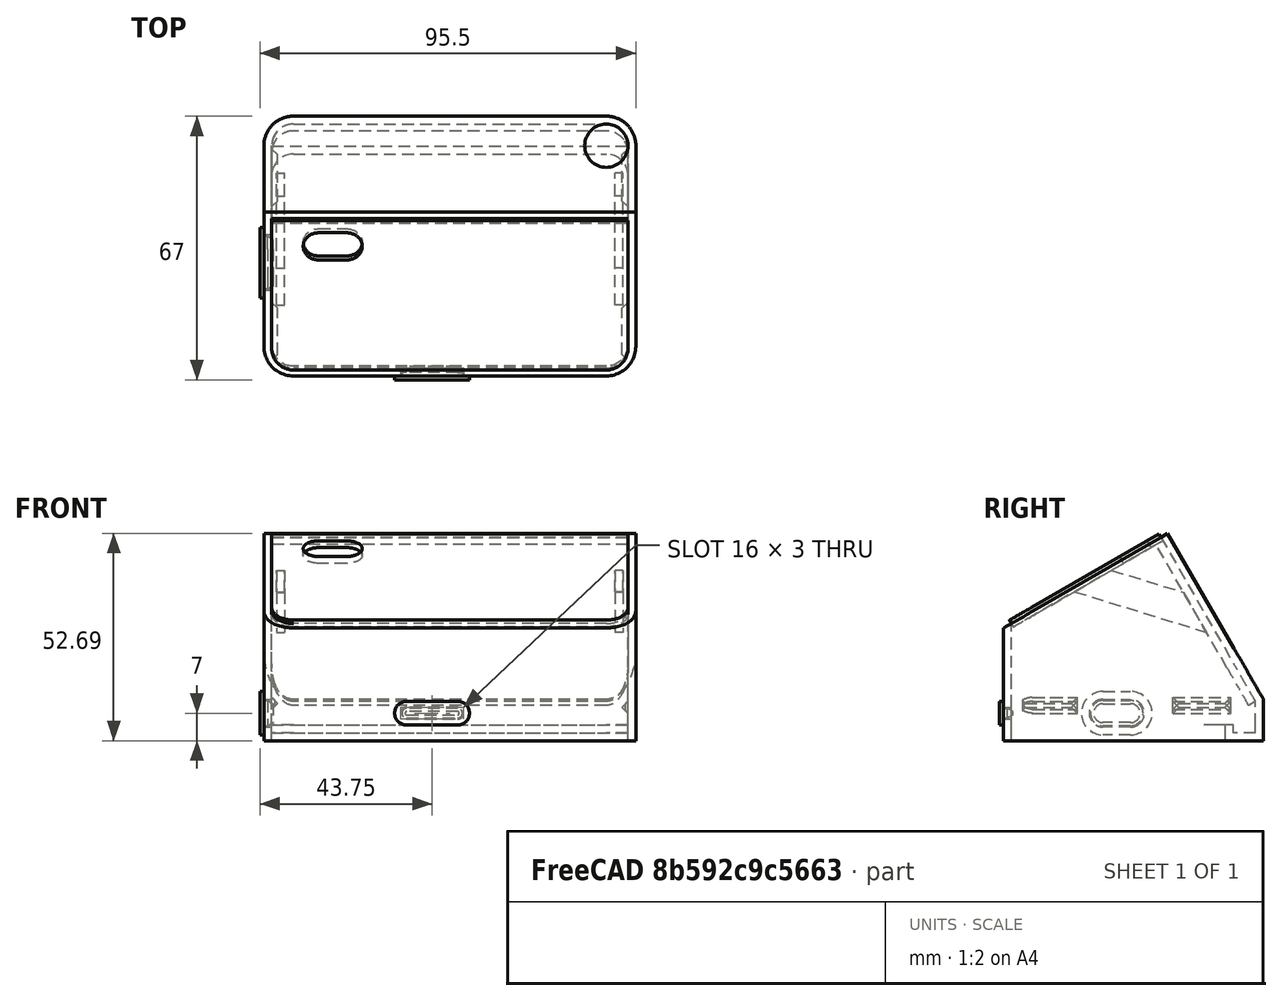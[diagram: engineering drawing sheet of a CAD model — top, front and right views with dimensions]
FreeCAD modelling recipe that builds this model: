
FCSTD DOCUMENT  (FreeCAD 0.21R33771 (Git))
Label: 2432S028_inner
License: All rights reserved
LicenseURL: http://en.wikipedia.org/wiki/All_rights_reserved
objects: Part::Extrusion×15, Sketcher::SketchObject×14, Part::Box×8, Part::Chamfer×6, Part::FeaturePython×6, Part::Cut×4, Mesh::Feature×4, Part::MultiCommon×2, Part::MultiFuse×1
note: 56 computed .brp shape members not serialized (recipe doc carries the construction recipe); baked Part::Feature solids carry a one-line shape summary decoded from their .brp

FEATURE [Sketcher::SketchObject] Sketch  label="Basis"
  FullyConstrained = true
  sketch-geometry (22):
    g0: LineSegment StartX=-39.75 StartY=33 StartZ=0 EndX=39.75 EndY=33 EndZ=0
    g1: LineSegment StartX=47.25 StartY=25.5 StartZ=0 EndX=47.25 EndY=-25.5 EndZ=0
    g2: LineSegment StartX=39.75 StartY=-33 StartZ=0 EndX=-39.75 EndY=-33 EndZ=0
    g3: LineSegment StartX=-47.25 StartY=-25.5 StartZ=0 EndX=-47.25 EndY=25.5 EndZ=0
    g4: ArcOfCircle CenterX=-39.75 CenterY=25.5 CenterZ=0 NormalX=0 NormalY=0 NormalZ=1 AngleXU=0 Radius=7.5 StartAngle=1.5708 EndAngle=3.14159
    g5: GeomPoint X=-47.25 Y=33 Z=0
    g6: ArcOfCircle CenterX=39.75 CenterY=25.5 CenterZ=0 NormalX=0 NormalY=0 NormalZ=1 AngleXU=0 Radius=7.5 StartAngle=0 EndAngle=1.5708
    g7: GeomPoint X=47.25 Y=33 Z=0
    g8: ArcOfCircle CenterX=39.75 CenterY=-25.5 CenterZ=0 NormalX=0 NormalY=0 NormalZ=1 AngleXU=0 Radius=7.5 StartAngle=4.71239 EndAngle=6.28319
    g9: GeomPoint X=47.25 Y=-33 Z=0
    g10: ArcOfCircle CenterX=-39.75 CenterY=-25.5 CenterZ=0 NormalX=0 NormalY=0 NormalZ=1 AngleXU=0 Radius=7.5 StartAngle=3.14159 EndAngle=4.71239
    g11: GeomPoint X=-47.25 Y=-33 Z=0
    g12: ArcOfCircle CenterX=39.75 CenterY=17.9 CenterZ=0 NormalX=0 NormalY=0 NormalZ=1 AngleXU=0 Radius=5.5 StartAngle=4e-16 EndAngle=1.5708
    g13: LineSegment StartX=45.25 StartY=17.9 StartZ=0 EndX=45.25 EndY=-25.5 EndZ=0
    g14: ArcOfCircle CenterX=39.75 CenterY=-25.5 CenterZ=0 NormalX=0 NormalY=0 NormalZ=1 AngleXU=0 Radius=5.5 StartAngle=4.71239 EndAngle=6.28319
    g15: LineSegment StartX=39.75 StartY=-31 StartZ=0 EndX=-39.75 EndY=-31 EndZ=0
    g16: ArcOfCircle CenterX=-39.75 CenterY=-25.5 CenterZ=0 NormalX=0 NormalY=0 NormalZ=1 AngleXU=0 Radius=5.5 StartAngle=3.14159 EndAngle=4.71239
    g17: LineSegment StartX=-45.25 StartY=-25.5 StartZ=0 EndX=-45.25 EndY=17.9 EndZ=0
    g18: ArcOfCircle CenterX=-39.75 CenterY=17.9 CenterZ=0 NormalX=0 NormalY=0 NormalZ=1 AngleXU=0 Radius=5.5 StartAngle=1.5708 EndAngle=3.14159
    g19: LineSegment StartX=-39.75 StartY=23.4 StartZ=0 EndX=39.75 EndY=23.4 EndZ=0
    g20: GeomPoint X=45.25 Y=23.4 Z=0
    g21: GeomPoint X=-45.25 Y=-31 Z=0
  constraints (50):
    c: Horizontal(g0)
    c: Horizontal(g2)
    c: Vertical(g1)
    c: Vertical(g3)
    c: DistanceY(g9,g7) = 66
    c: Symmetric(g5,g9,g-1)
    c: PointOnObject(g5,g0)
    c: PointOnObject(g5,g3)
    c: Tangent(g0,g4) = 1.5708
    c: Tangent(g3,g4) = 1.5708
    c: PointOnObject(g7,g0)
    c: PointOnObject(g7,g1)
    c: Tangent(g0,g6) = 1.5708
    c: Tangent(g1,g6) = 1.5708
    c: PointOnObject(g9,g1)
    c: PointOnObject(g9,g2)
    c: Tangent(g1,g8) = 1.5708
    c: Tangent(g2,g8) = 1.5708
    c: PointOnObject(g11,g2)
    c: PointOnObject(g11,g3)
    c: Tangent(g2,g10) = 1.5708
    c: Tangent(g3,g10) = 1.5708
    c: Equal(g8,g10)
    c: Equal(g10,g4)
    c: Equal(g4,g6)
    c: Tangent(g12,g13) = 1.5708
    c: Tangent(g13,g14) = 1.5708
    c: Tangent(g14,g15) = 1.5708
    c: Tangent(g15,g16) = 1.5708
    c: Tangent(g16,g17) = 1.5708
    c: Tangent(g17,g18) = 1.5708
    c: Tangent(g18,g19) = 1.5708
    c: Tangent(g19,g12) = 1.5708
    c: Horizontal(g15)
    c: Vertical(g13)
    c: Vertical(g17)
    c: Equal(g12,g14)
    c: Equal(g14,g16)
    c: Equal(g16,g18)
    c: PointOnObject(g20,g13)
    c: PointOnObject(g20,g19)
    c: PointOnObject(g21,g15)
    c: PointOnObject(g21,g17)
    c: DistanceY(g14,g12) = 54.4
    c: DistanceX(g17,g12) = 90.5
    c: Diameter(g12) = 11
    c: Symmetric(g12,g17,g-2)
    c: DistanceY(g2,g14) = 2
    c: Coincident(g10,g16)
    c: DistanceY(g18,g4) = 2.1
FEATURE [Part::Box] Box  label="Cube"
  AttacherType = Attacher::AttachEngine3D
  Height = 100
  Length = 100
  Placement = pos=(-50,39.3072,-0.4) rot=(1,0,0;0.523599rad)
  Width = 100
FEATURE [Sketcher::SketchObject] Sketch001
  ExternalGeometry = -> [Sketch]
  FullyConstrained = true
  sketch-geometry (20):
    g0: ArcOfCircle CenterX=-39.75 CenterY=25.5 CenterZ=0 NormalX=0 NormalY=0 NormalZ=1 AngleXU=0 Radius=7.5 StartAngle=1.5708 EndAngle=3.14159
    g1: LineSegment StartX=-39.75 StartY=33 StartZ=0 EndX=39.75 EndY=33 EndZ=0
    g2: ArcOfCircle CenterX=39.75 CenterY=25.5 CenterZ=0 NormalX=0 NormalY=0 NormalZ=1 AngleXU=0 Radius=7.5 StartAngle=1e-16 EndAngle=1.5708
    g3: LineSegment StartX=47.25 StartY=25.5 StartZ=0 EndX=47.25 EndY=-25.5 EndZ=0
    g4: ArcOfCircle CenterX=39.75 CenterY=-25.5 CenterZ=0 NormalX=0 NormalY=0 NormalZ=1 AngleXU=0 Radius=7.5 StartAngle=4.71239 EndAngle=6.28319
    g5: LineSegment StartX=39.75 StartY=-33 StartZ=0 EndX=-39.75 EndY=-33 EndZ=0
    g6: ArcOfCircle CenterX=-39.75 CenterY=-25.5 CenterZ=0 NormalX=0 NormalY=0 NormalZ=1 AngleXU=0 Radius=7.5 StartAngle=3.14159 EndAngle=4.71239
    g7: LineSegment StartX=-47.25 StartY=-25.5 StartZ=0 EndX=-47.25 EndY=25.5 EndZ=0
    g8: GeomPoint X=-47.25 Y=33 Z=0
    g9: GeomPoint X=47.25 Y=-33 Z=0
    g10: ArcOfCircle CenterX=-39.75 CenterY=17.9 CenterZ=0 NormalX=0 NormalY=0 NormalZ=1 AngleXU=0 Radius=5.5 StartAngle=1.5708 EndAngle=3.14159
    g11: LineSegment StartX=-39.75 StartY=23.4 StartZ=0 EndX=39.75 EndY=23.4 EndZ=0
    g12: ArcOfCircle CenterX=39.75 CenterY=17.9 CenterZ=0 NormalX=0 NormalY=0 NormalZ=1 AngleXU=0 Radius=5.5 StartAngle=0 EndAngle=1.5708
    g13: LineSegment StartX=45.25 StartY=17.9 StartZ=0 EndX=45.25 EndY=-25.5 EndZ=0
    g14: ArcOfCircle CenterX=39.75 CenterY=-25.5 CenterZ=0 NormalX=0 NormalY=0 NormalZ=1 AngleXU=0 Radius=5.5 StartAngle=4.71239 EndAngle=6.28319
    g15: LineSegment StartX=39.75 StartY=-31 StartZ=0 EndX=-39.75 EndY=-31 EndZ=0
    g16: ArcOfCircle CenterX=-39.75 CenterY=-25.5 CenterZ=0 NormalX=0 NormalY=0 NormalZ=1 AngleXU=0 Radius=5.5 StartAngle=3.14159 EndAngle=4.71239
    g17: LineSegment StartX=-45.25 StartY=-25.5 StartZ=0 EndX=-45.25 EndY=17.9 EndZ=0
    g18: GeomPoint X=-45.25 Y=23.4 Z=0
    g19: GeomPoint X=45.25 Y=-31 Z=0
  constraints (44):
    c: Tangent(g0,g1) = 1.5708
    c: Tangent(g1,g2) = 1.5708
    c: Tangent(g2,g3) = 1.5708
    c: Tangent(g3,g4) = 1.5708
    c: Tangent(g4,g5) = 1.5708
    c: Tangent(g5,g6) = 1.5708
    c: Tangent(g6,g7) = 1.5708
    c: Tangent(g7,g0) = 1.5708
    c: Horizontal(g1)
    c: Horizontal(g5)
    c: Vertical(g3)
    c: Vertical(g7)
    c: Equal(g0,g2)
    c: Equal(g2,g4)
    c: Equal(g4,g6)
    c: PointOnObject(g8,g1)
    c: PointOnObject(g8,g7)
    c: PointOnObject(g9,g3)
    c: PointOnObject(g9,g5)
    c: Coincident(g-6,g4)
    c: Coincident(g0,g-3)
    c: Horizontal(g-3,g0)
    c: Tangent(g10,g11) = 1.5708
    c: Tangent(g11,g12) = 1.5708
    c: Tangent(g12,g13) = 1.5708
    c: Tangent(g13,g14) = 1.5708
    c: Tangent(g14,g15) = 1.5708
    c: Tangent(g15,g16) = 1.5708
    c: Tangent(g16,g17) = 1.5708
    c: Tangent(g17,g10) = 1.5708
    c: Horizontal(g11)
    c: Horizontal(g15)
    c: Vertical(g13)
    c: Vertical(g17)
    c: Equal(g10,g12)
    c: Equal(g12,g14)
    c: Equal(g14,g16)
    c: PointOnObject(g18,g11)
    c: PointOnObject(g18,g17)
    c: PointOnObject(g19,g13)
    c: PointOnObject(g19,g15)
    c: Coincident(g14,g4)
    c: Coincident(g10,g-5)
    c: Horizontal(g-5,g10)
FEATURE [Part::Extrusion] Extrude
  Base = -> Sketch001
  Dir = (0,0,1)
  DirMode = 2
  FaceMakerClass = Part::FaceMakerBullseye
  LengthFwd = 2
  LengthRev = 0
  Solid = true
  Symmetric = false
FEATURE [Sketcher::SketchObject] Sketch002
  ExternalGeometry = -> [Sketch]
  FullyConstrained = true
  Placement = pos=(0,0,2) rot=(0,0,1;0rad)
  sketch-geometry (26):
    g0: ArcOfCircle CenterX=-39.75 CenterY=25.5 CenterZ=0 NormalX=0 NormalY=0 NormalZ=1 AngleXU=0 Radius=7.5 StartAngle=1.5708 EndAngle=3.14159
    g1: LineSegment StartX=-39.75 StartY=33 StartZ=0 EndX=39.75 EndY=33 EndZ=0
    g2: ArcOfCircle CenterX=39.75 CenterY=25.5 CenterZ=0 NormalX=0 NormalY=0 NormalZ=1 AngleXU=0 Radius=7.5 StartAngle=4e-16 EndAngle=1.5708
    g3: LineSegment StartX=47.25 StartY=25.5 StartZ=0 EndX=47.25 EndY=-25.5 EndZ=0
    g4: ArcOfCircle CenterX=39.75 CenterY=-25.5 CenterZ=0 NormalX=0 NormalY=0 NormalZ=1 AngleXU=0 Radius=7.5 StartAngle=4.71239 EndAngle=6.28319
    g5: LineSegment StartX=39.75 StartY=-33 StartZ=0 EndX=-39.75 EndY=-33 EndZ=0
    g6: ArcOfCircle CenterX=-39.75 CenterY=-25.5 CenterZ=0 NormalX=0 NormalY=0 NormalZ=1 AngleXU=0 Radius=7.5 StartAngle=3.14159 EndAngle=4.71239
    g7: LineSegment StartX=-47.25 StartY=-25.5 StartZ=0 EndX=-47.25 EndY=25.5 EndZ=0
    g8: GeomPoint X=-47.25 Y=33 Z=0
    g9: GeomPoint X=47.25 Y=-33 Z=0
    g10: ArcOfCircle CenterX=-39.75 CenterY=17.9 CenterZ=0 NormalX=0 NormalY=0 NormalZ=1 AngleXU=0 Radius=5.5 StartAngle=1.5708 EndAngle=3.14159
    g11: LineSegment StartX=-39.75 StartY=23.4 StartZ=0 EndX=39.75 EndY=23.4 EndZ=0
    g12: ArcOfCircle CenterX=39.75 CenterY=17.9 CenterZ=0 NormalX=0 NormalY=0 NormalZ=1 AngleXU=0 Radius=5.5 StartAngle=0 EndAngle=1.5708
    g13: LineSegment StartX=45.25 StartY=17.9 StartZ=0 EndX=45.25 EndY=-25.5 EndZ=0
    g14: ArcOfCircle CenterX=39.75 CenterY=-25.5 CenterZ=0 NormalX=0 NormalY=0 NormalZ=1 AngleXU=0 Radius=5.5 StartAngle=4.71239 EndAngle=6.28319
    g15: LineSegment StartX=39.75 StartY=-31 StartZ=0 EndX=-39.75 EndY=-31 EndZ=0
    g16: ArcOfCircle CenterX=-39.75 CenterY=-25.5 CenterZ=0 NormalX=0 NormalY=0 NormalZ=1 AngleXU=0 Radius=5.5 StartAngle=3.14159 EndAngle=4.71239
    g17: LineSegment StartX=-45.25 StartY=-25.5 StartZ=0 EndX=-45.25 EndY=17.9 EndZ=0
    g18: GeomPoint X=-45.25 Y=23.4 Z=0
    g19: GeomPoint X=45.25 Y=-31 Z=0
    g20: ArcOfCircle CenterX=-39.75 CenterY=25.5 CenterZ=0 NormalX=0 NormalY=0 NormalZ=1 AngleXU=0 Radius=5.5 StartAngle=1.5708 EndAngle=3.14159
    g21: LineSegment StartX=-39.75 StartY=31 StartZ=0 EndX=39.75 EndY=31 EndZ=0
    g22: ArcOfCircle CenterX=39.75 CenterY=25.5 CenterZ=0 NormalX=0 NormalY=0 NormalZ=1 AngleXU=0 Radius=5.5 StartAngle=0 EndAngle=1.5708
    g23: LineSegment StartX=-45.25 StartY=25.4 StartZ=0 EndX=45.25 EndY=25.4 EndZ=0
    g24: LineSegment StartX=-45.25 StartY=25.5 StartZ=0 EndX=-45.25 EndY=25.4 EndZ=0
    g25: LineSegment StartX=45.25 StartY=25.5 StartZ=0 EndX=45.25 EndY=25.4 EndZ=0
  constraints (62):
    c: Tangent(g0,g1) = 1.5708
    c: Tangent(g1,g2) = 1.5708
    c: Tangent(g2,g3) = 1.5708
    c: Tangent(g3,g4) = 1.5708
    c: Tangent(g4,g5) = 1.5708
    c: Tangent(g5,g6) = 1.5708
    c: Tangent(g6,g7) = 1.5708
    c: Tangent(g7,g0) = 1.5708
    c: Horizontal(g1)
    c: Horizontal(g5)
    c: Vertical(g3)
    c: Vertical(g7)
    c: Equal(g0,g2)
    c: Equal(g2,g4)
    c: Equal(g4,g6)
    c: PointOnObject(g8,g1)
    c: PointOnObject(g8,g7)
    c: PointOnObject(g9,g3)
    c: PointOnObject(g9,g5)
    c: Coincident(g4,g-6)
    c: Coincident(g0,g-3)
    c: Horizontal(g-3,g0)
    c: Tangent(g10,g11) = 1.5708
    c: Tangent(g11,g12) = 1.5708
    c: Tangent(g12,g13) = 1.5708
    c: Tangent(g13,g14) = 1.5708
    c: Tangent(g14,g15) = 1.5708
    c: Tangent(g15,g16) = 1.5708
    c: Tangent(g16,g17) = 1.5708
    c: Tangent(g17,g10) = 1.5708
    c: Horizontal(g11)
    c: Horizontal(g15)
    c: Vertical(g13)
    c: Vertical(g17)
    c: Equal(g10,g12)
    c: Equal(g12,g14)
    c: Equal(g14,g16)
    c: PointOnObject(g18,g11)
    c: PointOnObject(g18,g17)
    c: PointOnObject(g19,g13)
    c: PointOnObject(g19,g15)
    c: Coincident(g4,g14)
    c: Coincident(g10,g-5)
    c: Horizontal(g14,g-6)
    c: Coincident(g20,g0)
    c: Vertical(g0,g20)
    c: Horizontal(g0,g20)
    c: DistanceY(g20,g0) = 2
    c: Coincident(g21,g20)
    c: Horizontal(g21)
    c: Coincident(g22,g2)
    c: Coincident(g22,g21)
    c: Equal(g22,g20)
    c: Horizontal(g2,g22)
    c: Horizontal(g23)
    c: Coincident(g24,g20)
    c: Coincident(g24,g23)
    c: Vertical(g24)
    c: Coincident(g25,g22)
    c: Coincident(g25,g23)
    c: Vertical(g25)
    c: DistanceY(g10,g23) = 2
FEATURE [Part::Extrusion] Extrude001  label="Extrude_2mm"
  Base = -> Sketch002
  Dir = (0,0,1)
  DirMode = 2
  FaceMakerClass = Part::FaceMakerBullseye
  LengthFwd = 2
  LengthRev = 0
  Solid = true
  Symmetric = false
FEATURE [Sketcher::SketchObject] Sketch003
  ExternalGeometry = -> [Sketch]
  FullyConstrained = true
  Placement = pos=(0,0,4) rot=(0,0,1;0rad)
  sketch-geometry (20):
    g0: ArcOfCircle CenterX=-39.75 CenterY=25.5 CenterZ=0 NormalX=0 NormalY=0 NormalZ=1 AngleXU=0 Radius=7.5 StartAngle=1.5708 EndAngle=3.14159
    g1: LineSegment StartX=-39.75 StartY=33 StartZ=0 EndX=39.75 EndY=33 EndZ=0
    g2: ArcOfCircle CenterX=39.75 CenterY=25.5 CenterZ=0 NormalX=0 NormalY=0 NormalZ=1 AngleXU=0 Radius=7.5 StartAngle=0 EndAngle=1.5708
    g3: LineSegment StartX=47.25 StartY=25.5 StartZ=0 EndX=47.25 EndY=-25.5 EndZ=0
    g4: ArcOfCircle CenterX=39.75 CenterY=-25.5 CenterZ=0 NormalX=0 NormalY=0 NormalZ=1 AngleXU=0 Radius=7.5 StartAngle=4.71239 EndAngle=6.28319
    g5: LineSegment StartX=39.75 StartY=-33 StartZ=0 EndX=-39.75 EndY=-33 EndZ=0
    g6: ArcOfCircle CenterX=-39.75 CenterY=-25.5 CenterZ=0 NormalX=0 NormalY=0 NormalZ=1 AngleXU=0 Radius=7.5 StartAngle=3.14159 EndAngle=4.71239
    g7: LineSegment StartX=-47.25 StartY=-25.5 StartZ=0 EndX=-47.25 EndY=25.5 EndZ=0
    g8: GeomPoint X=-47.25 Y=33 Z=0
    g9: GeomPoint X=47.25 Y=-33 Z=0
    g10: ArcOfCircle CenterX=-39.75 CenterY=25.5 CenterZ=0 NormalX=0 NormalY=0 NormalZ=1 AngleXU=0 Radius=5.5 StartAngle=1.5708 EndAngle=3.14159
    g11: LineSegment StartX=-39.75 StartY=31 StartZ=0 EndX=39.75 EndY=31 EndZ=0
    g12: ArcOfCircle CenterX=39.75 CenterY=25.5 CenterZ=0 NormalX=0 NormalY=0 NormalZ=1 AngleXU=0 Radius=5.5 StartAngle=0 EndAngle=1.5708
    g13: LineSegment StartX=45.25 StartY=25.5 StartZ=0 EndX=45.25 EndY=-25.5 EndZ=0
    g14: ArcOfCircle CenterX=39.75 CenterY=-25.5 CenterZ=0 NormalX=0 NormalY=0 NormalZ=1 AngleXU=0 Radius=5.5 StartAngle=4.71239 EndAngle=6.28319
    g15: LineSegment StartX=39.75 StartY=-31 StartZ=0 EndX=-39.75 EndY=-31 EndZ=0
    g16: ArcOfCircle CenterX=-39.75 CenterY=-25.5 CenterZ=0 NormalX=0 NormalY=0 NormalZ=1 AngleXU=0 Radius=5.5 StartAngle=3.14159 EndAngle=4.71239
    g17: LineSegment StartX=-45.25 StartY=-25.5 StartZ=0 EndX=-45.25 EndY=25.5 EndZ=0
    g18: GeomPoint X=-45.25 Y=31 Z=0
    g19: GeomPoint X=45.25 Y=-31 Z=0
  constraints (45):
    c: Tangent(g0,g1) = 1.5708
    c: Tangent(g1,g2) = 1.5708
    c: Tangent(g2,g3) = 1.5708
    c: Tangent(g3,g4) = 1.5708
    c: Tangent(g4,g5) = 1.5708
    c: Tangent(g5,g6) = 1.5708
    c: Tangent(g6,g7) = 1.5708
    c: Tangent(g7,g0) = 1.5708
    c: Horizontal(g1)
    c: Horizontal(g5)
    c: Vertical(g3)
    c: Vertical(g7)
    c: Equal(g0,g2)
    c: Equal(g2,g4)
    c: Equal(g4,g6)
    c: PointOnObject(g8,g1)
    c: PointOnObject(g8,g7)
    c: PointOnObject(g9,g3)
    c: PointOnObject(g9,g5)
    c: Coincident(g-5,g4)
    c: Coincident(g0,g-3)
    c: Horizontal(g-3,g0)
    c: Tangent(g10,g11) = 1.5708
    c: Tangent(g12,g13) = 1.5708
    c: Tangent(g13,g14) = 1.5708
    c: Tangent(g14,g15) = 1.5708
    c: Tangent(g15,g16) = 1.5708
    c: Tangent(g16,g17) = 1.5708
    c: Tangent(g17,g10) = 1.5708
    c: Horizontal(g11)
    c: Horizontal(g15)
    c: Vertical(g13)
    c: Vertical(g17)
    c: Equal(g10,g12)
    c: Equal(g12,g14)
    c: Equal(g14,g16)
    c: PointOnObject(g18,g11)
    c: PointOnObject(g18,g17)
    c: PointOnObject(g19,g13)
    c: PointOnObject(g19,g15)
    c: Coincident(g14,g4)
    c: Coincident(g11,g12)
    c: Coincident(g0,g10)
    c: Horizontal(g15,g-6)
    c: Vertical(g12,g11)
FEATURE [Part::Extrusion] Extrude002  label="Extrude_4mm"
  Base = -> Sketch003
  Dir = (0,0,1)
  DirMode = 2
  FaceMakerClass = Part::FaceMakerBullseye
  LengthFwd = 10
  LengthRev = 0
  Solid = true
  Symmetric = false
FEATURE [Part::Extrusion] Extrude003  label="Extrude_6mm"
  Base = -> Sketch003
  Dir = (0,0,1)
  DirMode = 2
  FaceMakerClass = Part::FaceMakerBullseye
  LengthFwd = 52
  LengthRev = 0
  Solid = true
  Symmetric = false
FEATURE [Part::Box] Box001  label="Cube001"
  AttacherType = Attacher::AttachEngine3D
  Height = 100
  Length = 100
  Placement = pos=(-50,-49.5397,19.0874) rot=(1,0,0;0.523599rad)
  Width = 100
FEATURE [Part::Box] Box002  label="Cube002"
  AttacherType = Attacher::AttachEngine3D
  Height = 100
  Length = 100
  Placement = pos=(-50,37.5751,-1.4) rot=(1,0,0;0.523599rad)
  Width = 2
FEATURE [Sketcher::SketchObject] Sketch004
  ExternalGeometry = -> [Sketch]
  FullyConstrained = false
  sketch-geometry (12):
    g0: ArcOfCircle CenterX=-39.75 CenterY=25.5 CenterZ=0 NormalX=0 NormalY=0 NormalZ=1 AngleXU=0 Radius=7.5 StartAngle=1.5708 EndAngle=3.14159
    g1: LineSegment StartX=-39.75 StartY=33 StartZ=0 EndX=39.75 EndY=33 EndZ=0
    g2: ArcOfCircle CenterX=39.75 CenterY=25.5 CenterZ=0 NormalX=0 NormalY=0 NormalZ=1 AngleXU=0 Radius=7.5 StartAngle=1e-16 EndAngle=1.5708
    g3: LineSegment StartX=47.25 StartY=25.5 StartZ=0 EndX=47.25 EndY=-25.5 EndZ=0
    g4: ArcOfCircle CenterX=39.75 CenterY=-25.5 CenterZ=0 NormalX=0 NormalY=0 NormalZ=1 AngleXU=0 Radius=7.5 StartAngle=4.71239 EndAngle=6.28319
    g5: LineSegment StartX=39.75 StartY=-33 StartZ=0 EndX=-39.75 EndY=-33 EndZ=0
    g6: ArcOfCircle CenterX=-39.75 CenterY=-25.5 CenterZ=0 NormalX=0 NormalY=0 NormalZ=1 AngleXU=0 Radius=7.5 StartAngle=3.14159 EndAngle=4.71239
    g7: LineSegment StartX=-47.25 StartY=-25.5 StartZ=0 EndX=-47.25 EndY=25.5 EndZ=0
    g8: GeomPoint X=-47.25 Y=33 Z=0
    g9: GeomPoint X=47.25 Y=-33 Z=0
    g10: GeomPoint X=-22 Y=14 Z=0
    g11: GeomPoint X=22 Y=-30 Z=0
  constraints (22):
    c: Tangent(g0,g1) = 1.5708
    c: Tangent(g1,g2) = 1.5708
    c: Tangent(g2,g3) = 1.5708
    c: Tangent(g3,g4) = 1.5708
    c: Tangent(g4,g5) = 1.5708
    c: Tangent(g5,g6) = 1.5708
    c: Tangent(g6,g7) = 1.5708
    c: Tangent(g7,g0) = 1.5708
    c: Horizontal(g1)
    c: Horizontal(g5)
    c: Vertical(g3)
    c: Vertical(g7)
    c: Equal(g0,g2)
    c: Equal(g2,g4)
    c: Equal(g4,g6)
    c: PointOnObject(g8,g1)
    c: PointOnObject(g8,g7)
    c: PointOnObject(g9,g3)
    c: PointOnObject(g9,g5)
    c: Coincident(g0,g-3)
    c: Horizontal(g-3,g0)
    c: Coincident(g4,g-4)
FEATURE [Part::Extrusion] Extrude004
  Base = -> Sketch004
  Dir = (0,0,1)
  DirMode = 2
  FaceMakerClass = Part::FaceMakerBullseye
  LengthFwd = 56
  LengthRev = 0
  Solid = true
  Symmetric = false
FEATURE [Part::MultiCommon] Common
  Shapes = -> [Box002,Extrude004]
FEATURE [Part::MultiFuse] Fusion
  Shapes = -> [Common,Extrude,Extrude001,Extrude002,Extrude003]
FEATURE [Part::Cut] Cut
  Base = -> Fusion
  Tool = -> Box
FEATURE [Part::Cut] Cut001
  Base = -> Cut
  Tool = -> Box001
FEATURE [Part::Box] Box003  label="Cube003"
  AttacherType = Attacher::AttachEngine3D
  Height = 3
  Length = 1.5
  Placement = pos=(43.75,-29,7) rot=(0,0,1;0rad)
  Width = 14.7
FEATURE [Part::Chamfer] Chamfer
  Base = -> Box003
  Edges = 4 edges r=1.49: [Edge1,Edge2,Edge3,Edge4]
FEATURE [Part::Box] Box004  label="Cube004"
  AttacherType = Attacher::AttachEngine3D
  Height = 3
  Length = 1.5
  Placement = pos=(-45.25,-29,8) rot=(0,0,1;0rad)
  Width = 14.7
FEATURE [Part::Chamfer] Chamfer001
  Base = -> Box004
  Edges = 4 edges r=1.49: [Edge5,Edge6,Edge7,Edge8]
FEATURE [Sketcher::SketchObject] Sketch005  label="Basis001_bEZEL"
  FullyConstrained = true
  Placement = pos=(0,-2.75,0) rot=(0,1,0;3.14159rad)
  sketch-geometry (46):
    g0: ArcOfCircle CenterX=40 CenterY=22 CenterZ=0 NormalX=0 NormalY=0 NormalZ=1 AngleXU=0 Radius=3 StartAngle=4e-16 EndAngle=1.5708
    g1: LineSegment StartX=43 StartY=22 StartZ=0 EndX=43 EndY=-22 EndZ=0
    g2: ArcOfCircle CenterX=40 CenterY=-22 CenterZ=0 NormalX=0 NormalY=0 NormalZ=1 AngleXU=0 Radius=3 StartAngle=4.71239 EndAngle=6.28319
    g3: LineSegment StartX=40 StartY=-25 StartZ=0 EndX=-40 EndY=-25 EndZ=0
    g4: ArcOfCircle CenterX=-40 CenterY=-22 CenterZ=0 NormalX=0 NormalY=0 NormalZ=1 AngleXU=0 Radius=3 StartAngle=3.14159 EndAngle=4.71239
    g5: LineSegment StartX=-43 StartY=-22 StartZ=0 EndX=-43 EndY=22 EndZ=0
    g6: ArcOfCircle CenterX=-40 CenterY=22 CenterZ=0 NormalX=0 NormalY=0 NormalZ=1 AngleXU=0 Radius=3 StartAngle=1.5708 EndAngle=3.14159
    g7: LineSegment StartX=-40 StartY=25 StartZ=0 EndX=40 EndY=25 EndZ=0
    g8: GeomPoint X=43 Y=25 Z=0
    g9: GeomPoint X=-43 Y=-25 Z=0
    g10: Circle CenterX=-39 CenterY=21 CenterZ=0 NormalX=0 NormalY=0 NormalZ=1 AngleXU=0 Radius=1.6
    g11: Circle CenterX=-39 CenterY=-21 CenterZ=0 NormalX=0 NormalY=0 NormalZ=1 AngleXU=0 Radius=1.6
    g12: Circle CenterX=39 CenterY=21 CenterZ=0 NormalX=0 NormalY=0 NormalZ=1 AngleXU=0 Radius=1.6
    g13: Circle CenterX=39 CenterY=-21 CenterZ=0 NormalX=0 NormalY=0 NormalZ=1 AngleXU=0 Radius=1.6
    g14: LineSegment StartX=-35 StartY=25 StartZ=0 EndX=36 EndY=25 EndZ=0
    g15: LineSegment StartX=36 StartY=25 StartZ=0 EndX=36 EndY=-25 EndZ=0
    g16: LineSegment StartX=36 StartY=-25 StartZ=0 EndX=-35 EndY=-25 EndZ=0
    g17: LineSegment StartX=-35 StartY=-25 StartZ=0 EndX=-35 EndY=25 EndZ=0
    g18: LineSegment StartX=-40.4 StartY=-12 StartZ=0 EndX=-37.4 EndY=-12 EndZ=0
    g19: LineSegment StartX=-37.4 StartY=-12 StartZ=0 EndX=-37.4 EndY=-17 EndZ=0
    g20: LineSegment StartX=-37.4 StartY=-17 StartZ=0 EndX=-40.4 EndY=-17 EndZ=0
    g21: LineSegment StartX=-40.4 StartY=-17 StartZ=0 EndX=-40.4 EndY=-12 EndZ=0
    g22: LineSegment StartX=-2 StartY=-25 StartZ=0 EndX=11 EndY=-25 EndZ=0
    g23: LineSegment StartX=11 StartY=-25 StartZ=0 EndX=11 EndY=-28 EndZ=0
    g24: LineSegment StartX=11 StartY=-28 StartZ=0 EndX=-2 EndY=-28 EndZ=0
    g25: LineSegment StartX=-2 StartY=-28 StartZ=0 EndX=-2 EndY=-25 EndZ=0
    g26: LineSegment StartX=43 StartY=3 StartZ=0 EndX=53 EndY=3 EndZ=0
    g27: LineSegment StartX=53 StartY=3 StartZ=0 EndX=53 EndY=-6 EndZ=0
    g28: LineSegment StartX=53 StartY=-6 StartZ=0 EndX=43 EndY=-6 EndZ=0
    g29: LineSegment StartX=43 StartY=-6 StartZ=0 EndX=43 EndY=3 EndZ=0
    g30: LineSegment StartX=43 StartY=14 StartZ=0 EndX=45 EndY=14 EndZ=0
    g31: LineSegment StartX=45 StartY=14 StartZ=0 EndX=45 EndY=6 EndZ=0
    g32: LineSegment StartX=45 StartY=6 StartZ=0 EndX=43 EndY=6 EndZ=0
    g33: LineSegment StartX=43 StartY=6 StartZ=0 EndX=43 EndY=14 EndZ=0
    g34: LineSegment StartX=-31.5 StartY=-25 StartZ=0 EndX=-23.5 EndY=-25 EndZ=0
    g35: LineSegment StartX=-23.5 StartY=-25 StartZ=0 EndX=-23.5 EndY=-27 EndZ=0
    g36: LineSegment StartX=-23.5 StartY=-27 StartZ=0 EndX=-31.5 EndY=-27 EndZ=0
    g37: LineSegment StartX=-31.5 StartY=-27 StartZ=0 EndX=-31.5 EndY=-25 EndZ=0
    g38: LineSegment StartX=-16.5 StartY=-25 StartZ=0 EndX=-8.5 EndY=-25 EndZ=0
    g39: LineSegment StartX=-8.5 StartY=-25 StartZ=0 EndX=-8.5 EndY=-27 EndZ=0
    g40: LineSegment StartX=-8.5 StartY=-27 StartZ=0 EndX=-16.5 EndY=-27 EndZ=0
    g41: LineSegment StartX=-16.5 StartY=-27 StartZ=0 EndX=-16.5 EndY=-25 EndZ=0
    g42: LineSegment StartX=-33 StartY=22.5 StartZ=0 EndX=27 EndY=22.5 EndZ=0
    g43: LineSegment StartX=27 StartY=22.5 StartZ=0 EndX=27 EndY=-22.5 EndZ=0
    g44: LineSegment StartX=27 StartY=-22.5 StartZ=0 EndX=-33 EndY=-22.5 EndZ=0
    g45: LineSegment StartX=-33 StartY=-22.5 StartZ=0 EndX=-33 EndY=22.5 EndZ=0
  constraints (130):
    c: Tangent(g0,g1) = 1.5708
    c: Tangent(g1,g2) = 1.5708
    c: Tangent(g2,g3) = 1.5708
    c: Tangent(g3,g4) = 1.5708
    c: Tangent(g4,g5) = 1.5708
    c: Tangent(g5,g6) = 1.5708
    c: Tangent(g6,g7) = 1.5708
    c: Tangent(g7,g0) = 1.5708
    c: Horizontal(g3)
    c: Vertical(g1)
    c: Vertical(g5)
    c: Equal(g0,g2)
    c: Equal(g2,g4)
    c: Equal(g4,g6)
    c: PointOnObject(g8,g1)
    c: PointOnObject(g8,g7)
    c: PointOnObject(g9,g3)
    c: PointOnObject(g9,g5)
    c: DistanceY(g2,g0) = 50
    c: DistanceX(g5,g0) = 86
    c: Diameter(g0) = 6
    c: Symmetric(g6,g2,g-1)
    c: Horizontal(g7)
    c: Diameter(g10) = 3.2
    c: DistanceY(g10,g6) = 4
    c: DistanceX(g5,g10) = 4
    c: Equal(g10,g12)
    c: Horizontal(g10,g12)
    c: Vertical(g10,g11)
    c: Horizontal(g11,g13)
    c: Vertical(g13,g12)
    c: Equal(g10,g11)
    c: Equal(g11,g13)
    c: DistanceY(g2,g13) = 4
    c: DistanceX(g13,g1) = 4
    c: Coincident(g14,g15)
    c: Coincident(g15,g16)
    c: Coincident(g16,g17)
    c: Coincident(g17,g14)
    c: Horizontal(g14)
    c: Horizontal(g16)
    c: Vertical(g15)
    c: Vertical(g17)
    c: PointOnObject(g14,g7)
    c: PointOnObject(g16,g3)
    c: DistanceX(g14,g0) = 7
    c: DistanceX(g5,g14) = 8
    c: Coincident(g18,g19)
    c: Coincident(g19,g20)
    c: Coincident(g20,g21)
    c: Coincident(g21,g18)
    c: Horizontal(g18)
    c: Horizontal(g20)
    c: Vertical(g19)
    c: Vertical(g21)
    c: DistanceX(g20,g20) = 3
    c: DistanceY(g21,g21) = 5
    c: DistanceY(g3,g20) = 8
    c: DistanceX(g4,g20) = 2.6
    c: Coincident(g22,g23)
    c: Coincident(g23,g24)
    c: Coincident(g24,g25)
    c: Coincident(g25,g22)
    c: Horizontal(g22)
    c: Horizontal(g24)
    c: Vertical(g23)
    c: Vertical(g25)
    c: PointOnObject(g22,g3)
    c: DistanceX(g4,g22) = 41
    c: DistanceX(g22,g1) = 32
    c: DistanceY(g23,g23) = 3
    c: Coincident(g26,g27)
    c: Coincident(g27,g28)
    c: Coincident(g28,g29)
    c: Coincident(g29,g26)
    c: Horizontal(g26)
    c: Horizontal(g28)
    c: Vertical(g27)
    c: Vertical(g29)
    c: PointOnObject(g26,g1)
    c: DistanceY(g26,g0) = 22
    c: DistanceY(g2,g28) = 19
    c: DistanceX(g26,g26) = 10
    c: Coincident(g30,g31)
    c: Coincident(g31,g32)
    c: Coincident(g32,g33)
    c: Coincident(g33,g30)
    c: Horizontal(g30)
    c: Horizontal(g32)
    c: Vertical(g31)
    c: Vertical(g33)
    c: PointOnObject(g30,g1)
    c: DistanceY(g30,g0) = 11
    c: DistanceY(g2,g32) = 31
    c: DistanceX(g30,g30) = 2
    c: Coincident(g34,g35)
    c: Coincident(g35,g36)
    c: Coincident(g36,g37)
    c: Coincident(g37,g34)
    c: Horizontal(g34)
    c: Horizontal(g36)
    c: Vertical(g35)
    c: Vertical(g37)
    c: PointOnObject(g34,g3)
    c: Coincident(g38,g39)
    c: Coincident(g39,g40)
    c: Coincident(g40,g41)
    c: Coincident(g41,g38)
    c: Horizontal(g38)
    c: Horizontal(g40)
    c: Vertical(g39)
    c: Vertical(g41)
    c: PointOnObject(g38,g3)
    c: Equal(g31,g40)
    c: Equal(g40,g36)
    c: Equal(g32,g39)
    c: Equal(g39,g35)
    c: DistanceX(g4,g34) = 11.5
    c: DistanceX(g4,g38) = 26.5
    c: Coincident(g42,g43)
    c: Coincident(g43,g44)
    c: Coincident(g44,g45)
    c: Coincident(g45,g42)
    c: Horizontal(g42)
    c: Horizontal(g44)
    c: Vertical(g43)
    c: DistanceX(g44,g44) = 60
    c: DistanceY(g43,g43) = 45
    c: Symmetric(g42,g44,g-1)
    c: DistanceX(g14,g42) = 2
FEATURE [Sketcher::SketchObject] Sketch006
  ExternalGeometry = -> [Sketch005]
  FullyConstrained = true
  MapMode = 5
  Placement = pos=(0,-33,0) rot=(1,0,0;1.5708rad)
  Support = -> [Cut001]
  sketch-geometry (4):
    g0: ArcOfCircle CenterX=2 CenterY=7 CenterZ=0 NormalX=0 NormalY=0 NormalZ=1 AngleXU=0 Radius=1.5 StartAngle=4.71239 EndAngle=7.85398
    g1: ArcOfCircle CenterX=-11 CenterY=7 CenterZ=0 NormalX=0 NormalY=0 NormalZ=1 AngleXU=0 Radius=1.5 StartAngle=1.5708 EndAngle=4.71239
    g2: LineSegment StartX=2 StartY=8.5 StartZ=0 EndX=-11 EndY=8.5 EndZ=0
    g3: LineSegment StartX=-11 StartY=5.5 StartZ=0 EndX=2 EndY=5.5 EndZ=0
  constraints (10):
    c: Tangent(g0,g2) = -1.5708
    c: Tangent(g2,g1) = -1.5708
    c: Tangent(g1,g3) = -1.5708
    c: Tangent(g3,g0) = -1.5708
    c: Equal(g0,g1)
    c: Horizontal(g2)
    c: DistanceY(g-1,g1) = 7
    c: Diameter(g1) = 3
    c: Vertical(g1,g-3)
    c: Vertical(g0,g-3)
FEATURE [Part::Extrusion] Extrude005
  Base = -> Sketch006
  Dir = (0,-1,2e-16)
  DirMode = 2
  FaceMakerClass = Part::FaceMakerBullseye
  LengthFwd = 3
  LengthRev = 0
  Reversed = true
  Solid = true
  Symmetric = false
FEATURE [Sketcher::SketchObject] Sketch007
  ExternalGeometry = -> [Sketch005]
  FullyConstrained = true
  MapMode = 5
  Placement = pos=(-47.25,0,0) rot=(0.57735,-0.57735,-0.57735;2.0944rad)
  Support = -> [Cut001]
  sketch-geometry (6):
    g0: ArcOfCircle CenterX=0.75 CenterY=7 CenterZ=0 NormalX=0 NormalY=0 NormalZ=1 AngleXU=0 Radius=3.5 StartAngle=1.5708 EndAngle=4.71239
    g1: ArcOfCircle CenterX=7.75 CenterY=7 CenterZ=0 NormalX=0 NormalY=0 NormalZ=1 AngleXU=0 Radius=3.5 StartAngle=4.71239 EndAngle=7.85398
    g2: LineSegment StartX=0.75 StartY=3.5 StartZ=0 EndX=7.75 EndY=3.5 EndZ=0
    g3: LineSegment StartX=7.75 StartY=10.5 StartZ=0 EndX=0.75 EndY=10.5 EndZ=0
    g4: LineSegment StartX=-0.25 StartY=-6.5e-15 StartZ=0 EndX=0.75 EndY=3.5 EndZ=0
    g5: LineSegment StartX=7.75 StartY=3.5 StartZ=0 EndX=8.75 EndY=-6.7e-15 EndZ=0
  constraints (14):
    c: Tangent(g0,g2) = -1.5708
    c: Tangent(g2,g1) = -1.5708
    c: Tangent(g1,g3) = -1.5708
    c: Tangent(g3,g0) = -1.5708
    c: Equal(g0,g1)
    c: Horizontal(g2)
    c: DistanceY(g-1,g1) = 7
    c: Diameter(g1) = 7
    c: DistanceX(g3,g3) = 7
    c: Coincident(g4,g-3)
    c: Coincident(g4,g0)
    c: Coincident(g5,g1)
    c: Coincident(g5,g-3)
    c: Equal(g5,g4)
FEATURE [Part::Extrusion] Extrude006
  Base = -> Sketch007
  Dir = (-1,0,0)
  DirMode = 2
  FaceMakerClass = Part::FaceMakerBullseye
  LengthFwd = 3
  LengthRev = 0
  Reversed = true
  Solid = true
  Symmetric = false
FEATURE [Part::Box] Box005  label="Cube005"
  AttacherType = Attacher::AttachEngine3D
  Height = 3
  Length = 1.5
  Placement = pos=(43.75,10,7) rot=(0,0,1;0rad)
  Width = 14.7
FEATURE [Part::Chamfer] Chamfer002
  Base = -> Box005
  Edges = 4 edges r=1.49: [Edge1,Edge2,Edge3,Edge4]
FEATURE [Part::Box] Box006  label="Cube006"
  AttacherType = Attacher::AttachEngine3D
  Height = 3
  Length = 1.5
  Placement = pos=(-45.25,10,8) rot=(0,0,1;0rad)
  Width = 14.7
FEATURE [Part::Chamfer] Chamfer003
  Base = -> Box006
  Edges = 4 edges r=1.49: [Edge5,Edge6,Edge7,Edge8]
FEATURE [Part::Cut] Cut002
  Base = -> Cut001
  Tool = -> Extrude005
FEATURE [Part::Cut] Cut003
  Base = -> Cut002
  Tool = -> Extrude006
FEATURE [Part::FeaturePython] Connect  label="Main"  # WARN: FeaturePython — macro-defined, semantics opaque (R4)
  Objects = -> [Chamfer,Chamfer001,Chamfer002,Chamfer003,Cut003]
  Tolerance = 0
FEATURE [Mesh::Feature] Mesh  label="Main (Meshed)"
FEATURE [Sketcher::SketchObject] Sketch008
  ExternalGeometry = -> [Sketch007]
  FullyConstrained = true
  MapMode = 2
  Placement = pos=(-47.25,0,0) rot=(0.57735,-0.57735,-0.57735;2.0944rad)
  Support = -> [Sketch007]
  sketch-geometry (4):
    g0: ArcOfCircle CenterX=0.75 CenterY=7 CenterZ=0 NormalX=0 NormalY=0 NormalZ=1 AngleXU=0 Radius=3.2 StartAngle=1.5708 EndAngle=4.71239
    g1: ArcOfCircle CenterX=7.75 CenterY=7 CenterZ=0 NormalX=0 NormalY=0 NormalZ=1 AngleXU=0 Radius=3.2 StartAngle=4.71239 EndAngle=7.85398
    g2: LineSegment StartX=0.75 StartY=3.8 StartZ=0 EndX=7.75 EndY=3.8 EndZ=0
    g3: LineSegment StartX=7.75 StartY=10.2 StartZ=0 EndX=0.75 EndY=10.2 EndZ=0
  constraints (9):
    c: Radius(g-3) = 3.5
    c: Tangent(g0,g2) = -1.5708
    c: Tangent(g2,g1) = -1.5708
    c: Tangent(g1,g3) = -1.5708
    c: Tangent(g3,g0) = -1.5708
    c: Equal(g0,g1)
    c: Coincident(g0,g-3)
    c: Coincident(g1,g-4)
    c: Radius(g0) = 3.2
FEATURE [Part::Extrusion] Extrude007
  Base = -> Sketch008
  Dir = (-1,0,0)
  DirMode = 2
  FaceMakerClass = Part::FaceMakerBullseye
  LengthFwd = 2.4
  LengthRev = 0
  Reversed = true
  Solid = true
  Symmetric = false
FEATURE [Part::Chamfer] Chamfer004
  Base = -> Extrude007
  Edges = 1 edges: [Edge7 r1=1.5 r2=0.8]
FEATURE [Sketcher::SketchObject] Sketch009
  ExternalGeometry = -> [Sketch007]
  FullyConstrained = true
  MapMode = 2
  Placement = pos=(-47.25,0,0) rot=(0.57735,-0.57735,-0.57735;2.0944rad)
  Support = -> [Sketch007]
  sketch-geometry (4):
    g0: ArcOfCircle CenterX=0.75 CenterY=7 CenterZ=0 NormalX=0 NormalY=0 NormalZ=1 AngleXU=0 Radius=5.5 StartAngle=1.5708 EndAngle=4.71239
    g1: ArcOfCircle CenterX=7.75 CenterY=7 CenterZ=0 NormalX=0 NormalY=0 NormalZ=1 AngleXU=0 Radius=5.5 StartAngle=4.71239 EndAngle=7.85398
    g2: LineSegment StartX=0.75 StartY=1.5 StartZ=0 EndX=7.75 EndY=1.5 EndZ=0
    g3: LineSegment StartX=7.75 StartY=12.5 StartZ=0 EndX=0.75 EndY=12.5 EndZ=0
  constraints (9):
    c: Radius(g-3) = 3.5
    c: Tangent(g0,g2) = -1.5708
    c: Tangent(g2,g1) = -1.5708
    c: Tangent(g1,g3) = -1.5708
    c: Tangent(g3,g0) = -1.5708
    c: Equal(g0,g1)
    c: Coincident(g0,g-3)
    c: Coincident(g1,g-4)
    c: Radius(g0) = 5.5
FEATURE [Part::Extrusion] Extrude008
  Base = -> Sketch009
  Dir = (-1,0,0)
  DirMode = 2
  FaceMakerClass = Part::FaceMakerBullseye
  LengthFwd = 1
  LengthRev = 0
  Solid = true
  Symmetric = false
FEATURE [Part::FeaturePython] Connect001  label="Deckel_USB"  # WARN: FeaturePython — macro-defined, semantics opaque (R4)
  Objects = -> [Chamfer004,Extrude008]
  Tolerance = 0
FEATURE [Mesh::Feature] Mesh001  label="Deckel_USB (Meshed)"
  Placement = pos=(-57.5,0,48.25) rot=(0,1,0;4.71239rad)
FEATURE [Sketcher::SketchObject] Sketch010
  ExternalGeometry = -> [Sketch006]
  FullyConstrained = true
  MapMode = 2
  Placement = pos=(0,-33,0) rot=(1,0,0;1.5708rad)
  Support = -> [Sketch006]
  sketch-geometry (4):
    g0: ArcOfCircle CenterX=-11 CenterY=7 CenterZ=0 NormalX=0 NormalY=0 NormalZ=1 AngleXU=0 Radius=1.2 StartAngle=1.5708 EndAngle=4.71239
    g1: ArcOfCircle CenterX=2 CenterY=7 CenterZ=0 NormalX=0 NormalY=0 NormalZ=1 AngleXU=0 Radius=1.2 StartAngle=4.71239 EndAngle=7.85398
    g2: LineSegment StartX=-11 StartY=5.8 StartZ=0 EndX=2 EndY=5.8 EndZ=0
    g3: LineSegment StartX=2 StartY=8.2 StartZ=0 EndX=-11 EndY=8.2 EndZ=0
  constraints (9):
    c: Tangent(g0,g2) = -1.5708
    c: Tangent(g2,g1) = -1.5708
    c: Tangent(g1,g3) = -1.5708
    c: Tangent(g3,g0) = -1.5708
    c: Equal(g0,g1)
    c: Coincident(g0,g-3)
    c: Coincident(g1,g-4)
    c: Radius(g-3) = 1.5
    c: Radius(g0) = 1.2
FEATURE [Part::Extrusion] Extrude009
  Base = -> Sketch010
  Dir = (0,-1,2e-16)
  DirMode = 2
  FaceMakerClass = Part::FaceMakerBullseye
  LengthFwd = 2.4
  LengthRev = 0
  Reversed = true
  Solid = true
  Symmetric = false
FEATURE [Sketcher::SketchObject] Sketch011
  ExternalGeometry = -> [Sketch006]
  FullyConstrained = true
  MapMode = 2
  Placement = pos=(0,-33,0) rot=(1,0,0;1.5708rad)
  Support = -> [Sketch006]
  sketch-geometry (4):
    g0: ArcOfCircle CenterX=-11 CenterY=7 CenterZ=0 NormalX=0 NormalY=0 NormalZ=1 AngleXU=0 Radius=3 StartAngle=1.5708 EndAngle=4.71239
    g1: ArcOfCircle CenterX=2 CenterY=7 CenterZ=0 NormalX=0 NormalY=0 NormalZ=1 AngleXU=0 Radius=3 StartAngle=4.71239 EndAngle=7.85398
    g2: LineSegment StartX=-11 StartY=4 StartZ=0 EndX=2 EndY=4 EndZ=0
    g3: LineSegment StartX=2 StartY=10 StartZ=0 EndX=-11 EndY=10 EndZ=0
  constraints (9):
    c: Tangent(g0,g2) = -1.5708
    c: Tangent(g2,g1) = -1.5708
    c: Tangent(g1,g3) = -1.5708
    c: Tangent(g3,g0) = -1.5708
    c: Equal(g0,g1)
    c: Coincident(g0,g-3)
    c: Coincident(g1,g-4)
    c: Radius(g-3) = 1.5
    c: Radius(g0) = 3
FEATURE [Part::Extrusion] Extrude010
  Base = -> Sketch011
  Dir = (0,-1,2e-16)
  DirMode = 2
  FaceMakerClass = Part::FaceMakerBullseye
  LengthFwd = 1
  LengthRev = 0
  Solid = true
  Symmetric = false
FEATURE [Part::FeaturePython] Connect002  label="Deckel MicroSD"  # WARN: FeaturePython — macro-defined, semantics opaque (R4)
  Objects = -> [Extrude009,Extrude010]
  Tolerance = 0
FEATURE [Part::Chamfer] Chamfer005  label="Deckel MicroSD001"
  Base = -> Connect002
  Edges = 1 edges: [Edge11 r1=0.8 r2=1.5]
FEATURE [Mesh::Feature] Mesh003  label="Deckel MicroSD (Meshed)"
  Placement = pos=(0,-35.5,34) rot=(1,0,0;1.5708rad)
FEATURE [Part::Box] Box007  label="Cube007"
  AttacherType = Attacher::AttachEngine3D
  Height = 1
  Length = 100
  Placement = pos=(-50,-49.5397,19.0874) rot=(1,0,0;0.523599rad)
  Width = 100
FEATURE [Part::MultiCommon] Common001
  Shapes = -> [Cut,Box007]
FEATURE [Part::FeaturePython] Facebinder  # WARN: FeaturePython — macro-defined, semantics opaque (R4)
  Area = 569.521
  Extrusion = 0
  Faces = -> [Common001]
  RemoveSplitter = false
  Sew = false
FEATURE [Sketcher::SketchObject] Sketch012
  FullyConstrained = false
  Placement = pos=(0,-20.65,35.7668) rot=(1,0,0;3.66519rad)
  sketch-geometry (20):
    g0: LineSegment StartX=-47.25 StartY=5.6003 StartZ=0 EndX=-47.25 EndY=-31.841 EndZ=0
    g1: LineSegment StartX=-47.25 StartY=-31.841 StartZ=0 EndX=-47.25 EndY=-33.841 EndZ=0
    g2: LineSegment StartX=-47.25 StartY=-33.841 StartZ=0 EndX=-45.25 EndY=-33.841 EndZ=0
    g3: LineSegment StartX=-45.25 StartY=-33.841 StartZ=0 EndX=45.25 EndY=-33.841 EndZ=0
    g4: LineSegment StartX=45.25 StartY=-33.841 StartZ=0 EndX=47.25 EndY=-33.841 EndZ=0
    g5: LineSegment StartX=47.25 StartY=-33.841 StartZ=0 EndX=47.25 EndY=-31.841 EndZ=0
    g6: LineSegment StartX=47.25 StartY=-31.841 StartZ=0 EndX=47.25 EndY=5.6003 EndZ=0
    g7: ArcOfEllipse CenterX=39.75 CenterY=5.6003 CenterZ=0 NormalX=0 NormalY=-1e-16 NormalZ=1 MajorRadius=8.66025 MinorRadius=7.5 AngleXU=0 StartAngle=4.71239 EndAngle=6.28319
    g8: LineSegment StartX=39.75 StartY=14.2606 StartZ=0 EndX=-39.75 EndY=14.2606 EndZ=0
    g9: ArcOfEllipse CenterX=-39.75 CenterY=5.6003 CenterZ=0 NormalX=0 NormalY=-1e-16 NormalZ=1 MajorRadius=8.66025 MinorRadius=7.5 AngleXU=0 StartAngle=0 EndAngle=1.5708
    g10: ArcOfEllipse CenterX=-39.7356 CenterY=5.58989 CenterZ=0 NormalX=0 NormalY=-1e-16 NormalZ=1 MajorRadius=6.36708 MinorRadius=5.51431 AngleXU=0.0120287 StartAngle=6.27107 EndAngle=7.8407
    g11: LineSegment StartX=39.75 StartY=11.9568 StartZ=0 EndX=-39.7453 EndY=11.9568 EndZ=0
    g12: ArcOfEllipse CenterX=39.7498 CenterY=5.60031 CenterZ=0 NormalX=0 NormalY=-1e-16 NormalZ=1 MajorRadius=6.35653 MinorRadius=5.50656 AngleXU=-7.28146e-05 StartAngle=4.71245 EndAngle=6.28323
    g13: LineSegment StartX=45.2563 StartY=-31.84 StartZ=0 EndX=45.2563 EndY=5.6003 EndZ=0
    g14: LineSegment StartX=-45.25 StartY=-31.84 StartZ=0 EndX=45.2563 EndY=-31.84 EndZ=0
    g15: LineSegment StartX=-45.25 StartY=5.60814 StartZ=0 EndX=-45.25 EndY=-31.84 EndZ=0
    g16: ArcOfCircle CenterX=-26.25 CenterY=-24.34 CenterZ=0 NormalX=0 NormalY=0 NormalZ=1 AngleXU=0 Radius=4 StartAngle=4.71239 EndAngle=7.85398
    g17: ArcOfCircle CenterX=-33.25 CenterY=-24.34 CenterZ=0 NormalX=0 NormalY=0 NormalZ=1 AngleXU=0 Radius=4 StartAngle=1.5708 EndAngle=4.71239
    g18: LineSegment StartX=-26.25 StartY=-20.34 StartZ=0 EndX=-33.25 EndY=-20.34 EndZ=0
    g19: LineSegment StartX=-33.25 StartY=-28.34 StartZ=0 EndX=-26.25 EndY=-28.34 EndZ=0
  constraints (40):
    c: Vertical(g0)
    c: Coincident(g0,g1)
    c: Vertical(g1)
    c: Coincident(g1,g2)
    c: Horizontal(g2)
    c: Coincident(g2,g3)
    c: Horizontal(g3)
    c: Coincident(g3,g4)
    c: Horizontal(g4)
    c: Coincident(g4,g5)
    c: Vertical(g5)
    c: Coincident(g5,g6)
    c: Vertical(g6)
    c: Coincident(g6,g7)
    c: Coincident(g7,g8)
    c: Horizontal(g8)
    c: Coincident(g8,g9)
    c: Coincident(g9,g0)
    c: Coincident(g10,g11)
    c: Horizontal(g11)
    c: Coincident(g11,g12)
    c: Coincident(g12,g13)
    c: Vertical(g13)
    c: Coincident(g13,g14)
    c: Horizontal(g14)
    c: Coincident(g14,g15)
    c: Vertical(g15)
    c: Coincident(g15,g10)
    c: Tangent(g16,g18) = -1.5708
    c: Tangent(g18,g17) = -1.5708
    c: Tangent(g17,g19) = -1.5708
    c: Tangent(g19,g16) = -1.5708
    c: Equal(g16,g17)
    c: Horizontal(g18)
    c: DistanceX(g18,g18) = 7
    c: Radius(g16) = 4
    c: DistanceY(g14,g-1) = 31.84
    c: DistanceX(g14,g-1) = 45.25
    c: DistanceY(g14,g17) = 3.5
    c: DistanceX(g14,g17) = 12
FEATURE [Part::Extrusion] Extrude011
  Base = -> Sketch012
  Dir = (0,0.5,-0.866025)
  DirMode = 2
  FaceMakerClass = Part::FaceMakerBullseye
  LengthFwd = 2
  LengthRev = 0
  Solid = true
  Symmetric = true
FEATURE [Part::FeaturePython] Facebinder001  # WARN: FeaturePython — macro-defined, semantics opaque (R4)
  Area = 4331.58
  Extrusion = 0
  Faces = -> [Cut003]
  RemoveSplitter = false
  Sew = false
FEATURE [Part::Extrusion] Extrude012
  Base = -> Facebinder001
  Dir = (0,-0.866025,-0.5)
  DirMode = 2
  FaceMakerClass = Part::FaceMakerBullseye
  LengthFwd = 2
  LengthRev = 0
  Solid = false
  Symmetric = false
FEATURE [Sketcher::SketchObject] Sketch013
  ExternalGeometry = -> [Extrude011,Extrude012]
  FullyConstrained = false
  Placement = pos=(44,0,0) rot=(0.57735,0.57735,0.57735;2.0944rad)
  sketch-geometry (5):
    g0: LineSegment StartX=-15.021 StartY=37.8621 StartZ=0 EndX=18.5713 EndY=27.5156 EndZ=0
    g1: LineSegment StartX=-5.56613 StartY=43.3208 StartZ=0 EndX=12.6931 EndY=37.697 EndZ=0
    g2: LineSegment StartX=-15.021 StartY=37.8621 StartZ=0 EndX=-5.56613 EndY=43.3208 EndZ=0
    g3: LineSegment StartX=12.6931 StartY=37.697 StartZ=0 EndX=18.5713 EndY=27.5156 EndZ=0
    g4: LineSegment StartX=-6.18275 StartY=43.5107 StartZ=0 EndX=-8.53759 EndY=35.8652 EndZ=0
  constraints (15):
    c: PointOnObject(g0,g-3)
    c: PointOnObject(g0,g-4)
    c: PointOnObject(g1,g-3)
    c: PointOnObject(g1,g-4)
    c: Parallel(g1,g0)
    c: Coincident(g2,g0)
    c: Coincident(g2,g1)
    c: Coincident(g3,g1)
    c: Coincident(g3,g0)
    c: PointOnObject(g4,g1)
    c: PointOnObject(g4,g0)
    c: Perpendicular(g4,g1)
    c: Distance(g4) = 8
    c: Distance(g1,g-3) = 15
    c: Distance(g-4,g1) = 15
FEATURE [Part::Extrusion] Extrude013
  Base = -> Sketch013
  Dir = (1,-2e-16,2e-16)
  DirMode = 2
  FaceMakerClass = Part::FaceMakerBullseye
  LengthFwd = 2
  LengthRev = 0
  Reversed = true
  Solid = true
  Symmetric = false
FEATURE [Part::Extrusion] Extrude014
  Base = -> Sketch013
  Dir = (1,-2e-16,2e-16)
  DirMode = 2
  FaceMakerClass = Part::FaceMakerBullseye
  LengthFwd = 2
  LengthRev = 0
  Placement = pos=(-88,0,0) rot=(0,0,1;0rad)
  Solid = true
  Symmetric = false
FEATURE [Part::FeaturePython] Connect003  # WARN: FeaturePython — macro-defined, semantics opaque (R4)
  Objects = -> [Extrude011,Extrude012,Extrude013,Extrude014]
  Tolerance = 0
FEATURE [Mesh::Feature] Mesh004  label="inner"
  Placement = pos=(0,-72.5711,42.3031) rot=(1,0,0;2.61799rad)
